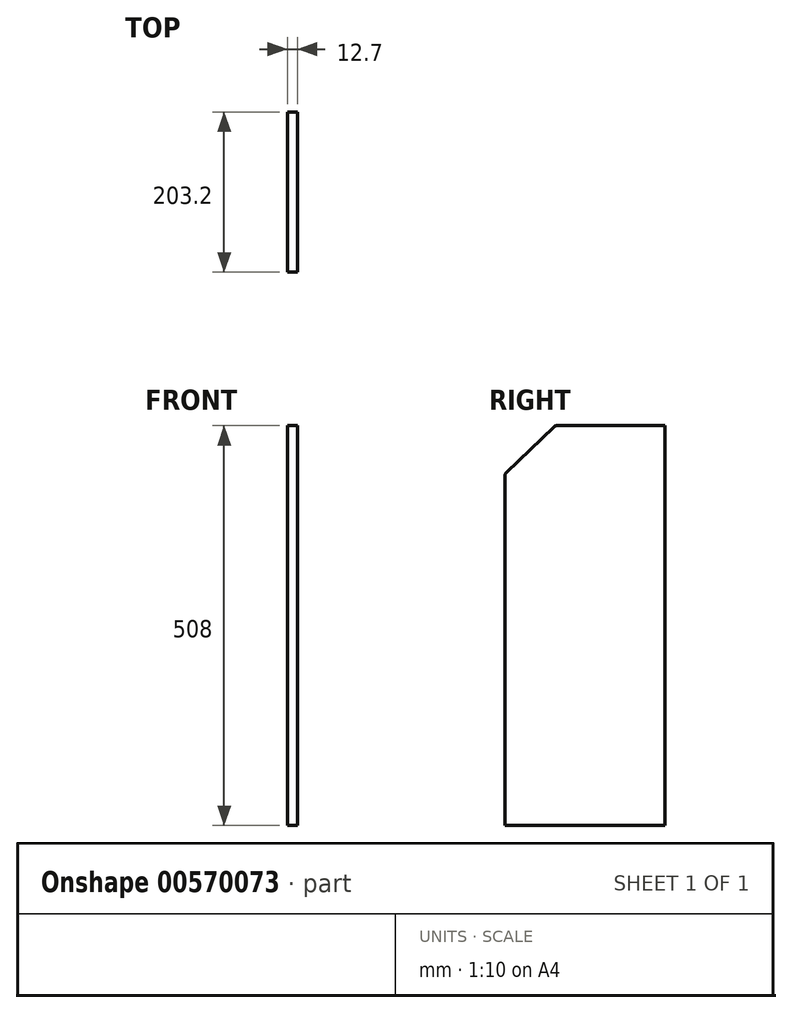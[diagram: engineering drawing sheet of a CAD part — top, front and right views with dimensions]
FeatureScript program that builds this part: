
annotation { "Feature Type Name" : "Feature", "Feature Type Description" : "" }
export const myFeature = defineFeature(function(context is Context, id is Id, definition is map)
    precondition{}
    {
        {
            var Q0;
            Q0=qCreatedBy(makeId("Right.planeOp"),FACE);
            var sketch = newSketch(context, id + "F0", { "sketchPlane" : qUnion([Q0])});
            skLineSegment(sketch, "E0", {"start": v(0, 0) * mm, "end": v(203.2, 0) * mm});
            skLineSegment(sketch, "E1", {"start": v(203.2, 0) * mm, "end": v(203.2, 444.05) * mm});
            skLineSegment(sketch, "E2", {"start": v(136.83, 508) * mm, "end": v(0, 508) * mm});
            skLineSegment(sketch, "E3", {"start": v(0, 508) * mm, "end": v(0, 0) * mm});
            skLineSegment(sketch, "E4", {"start": v(141.23, 506.23) * mm, "end": v(201.25, 448.63) * mm});
            skArc(sketch, "E5.filletArc", {"start": v(141.23, 506.23) * mm, "mid": v(139.2, 507.54) * mm, "end": v(136.83, 508) * mm});
            skPoint(sketch, "E6.newPointB", {"position": v(203.2, 508) * mm});
            skArc(sketch, "E6.filletArc", {"start": v(203.2, 444.05) * mm, "mid": v(202.7, 446.54) * mm, "end": v(201.25, 448.63) * mm});
            skSolve(sketch);
        }
        {
            var Q0;
            Q0 = qSketchRegion(id + "F0", true);
            extrude(context, id + "F1", {"entities" : qUnion([Q0]), "depth" : 12.7 * mm, "offsetDistance" : 25.4 * mm});
        }
        {
            var Q0;
            Q0=makeQuery(id+"F1.opExtrude","SWEPT_BODY",BODY,{"disambiguationData":[OSD([sQuery(id+"F0.wireOp",EDGE,"E0"),sQuery(id+"F0.wireOp",EDGE,"E1"),sQuery(id+"F0.wireOp",EDGE,"E2"),sQuery(id+"F0.wireOp",EDGE,"E3"),sQuery(id+"F0.wireOp",EDGE,"E4"),sQuery(id+"F0.wireOp",EDGE,"E5.filletArc"),sQuery(id+"F0.wireOp",EDGE,"E6.filletArc")])]});
            var Q1;
            Q1=makeQuery(id+"F1.opExtrude","CAP_EDGE",EDGE,{"disambiguationData":[OSD([sQuery(id+"F0.wireOp",EDGE,"E3")])],"isStart":false});
            transform(context, id + "F2", {"entities" : qUnion([Q0]), "transformType" : TransformType.ROTATION, "transformAxis" : qUnion([Q1]), "angle" : 180 * degree, "makeCopy" : false});
        }
    });
